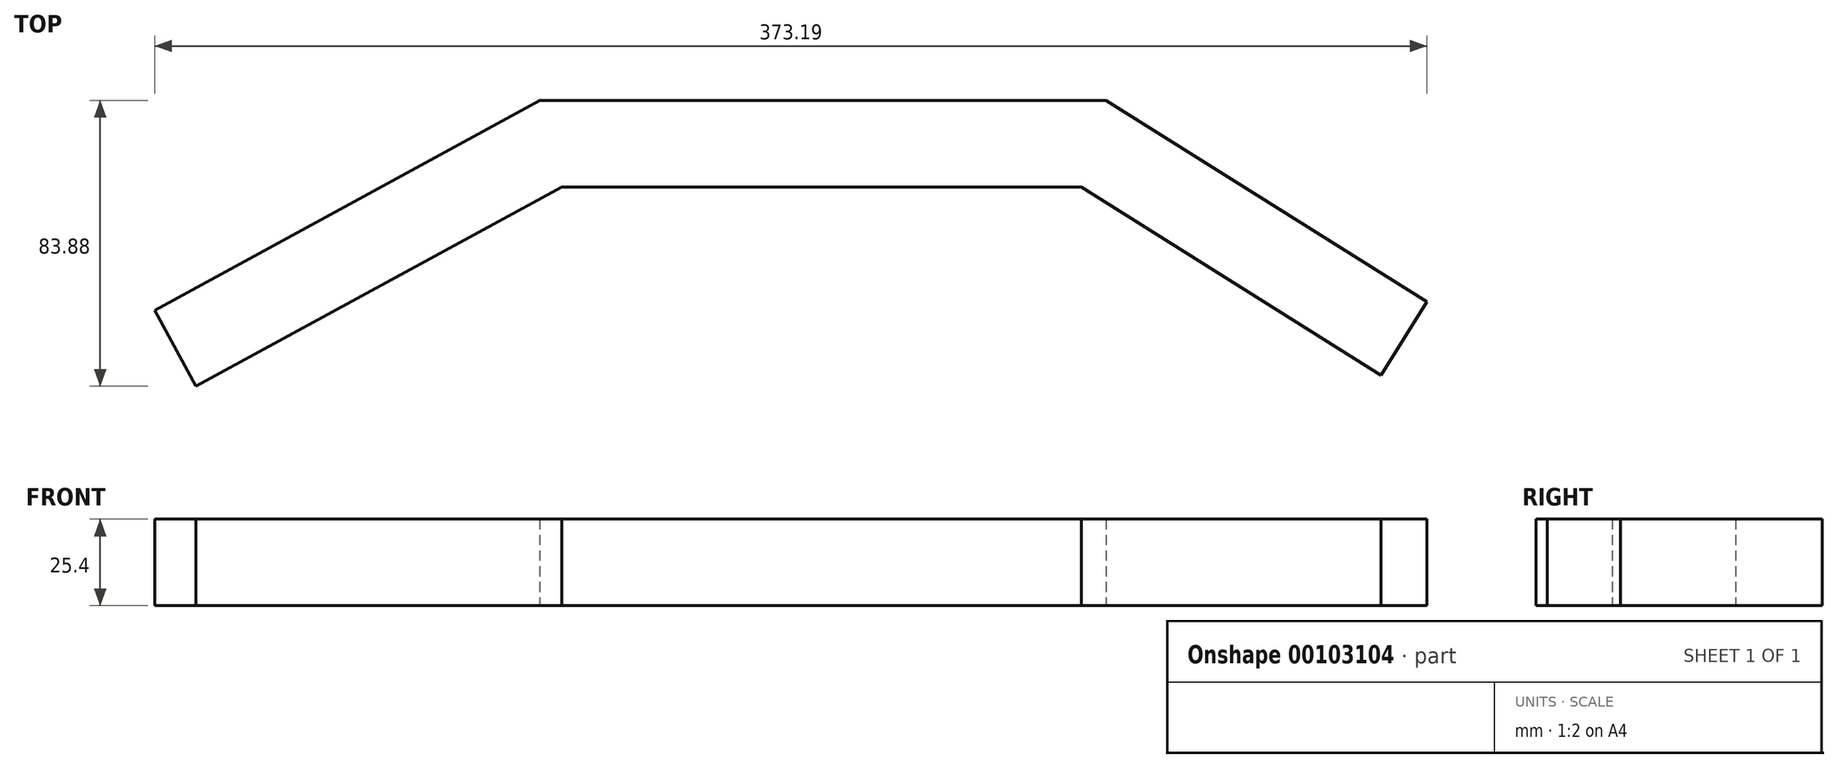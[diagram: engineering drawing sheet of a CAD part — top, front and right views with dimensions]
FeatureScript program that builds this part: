
annotation { "Feature Type Name" : "Feature", "Feature Type Description" : "" }
export const myFeature = defineFeature(function(context is Context, id is Id, definition is map)
    precondition{}
    {
        {
            var Q0;
            Q0=qCreatedBy(makeId("Top.planeOp"),FACE);
            var sketch = newSketch(context, id + "F0", { "sketchPlane" : qUnion([Q0])});
            skLineSegment(sketch, "E0", {"start": v(-135.87, -39.35) * mm, "end": v(-28.58, 19.13) * mm});
            skLineSegment(sketch, "E1", {"start": v(-28.58, 19.13) * mm, "end": v(123.72, 19.13) * mm});
            skLineSegment(sketch, "E2", {"start": v(123.72, 19.13) * mm, "end": v(211.65, -36.1) * mm});
            skLineSegment(sketch, "E3.0", {"start": v(131.03, 44.53) * mm, "end": v(225.16, -14.6) * mm});
            skLineSegment(sketch, "E3.1", {"start": v(-35.05, 44.53) * mm, "end": v(131.03, 44.53) * mm});
            skLineSegment(sketch, "E3.2", {"start": v(-148.03, -17.05) * mm, "end": v(-35.05, 44.53) * mm});
            skLineSegment(sketch, "E4", {"start": v(-148.03, -17.05) * mm, "end": v(-135.87, -39.35) * mm});
            skLineSegment(sketch, "E5", {"start": v(225.16, -14.6) * mm, "end": v(211.65, -36.1) * mm});
            skSolve(sketch);
        }
        {
            var Q0;
            Q0=makeQuery(id+"F0.imprint","IMPRINT",FACE,{"disambiguationData":[TD([[makeQuery(id+"F0.imprint","IMPRINT",EDGE,{"derivedFrom":sQuery(id+"F0.wireOp",EDGE,"E0")}),1.0]])]});
            extrude(context, id + "F1", {"entities" : qUnion([Q0]), "depth" : 25.4 * mm});
        }
    });
